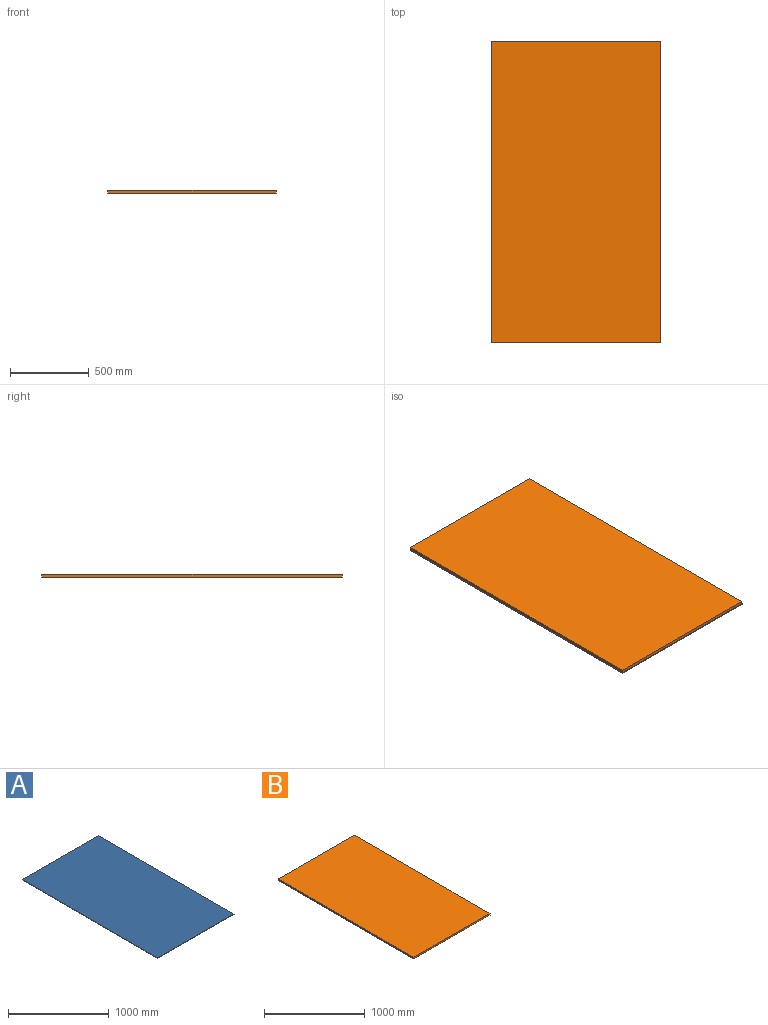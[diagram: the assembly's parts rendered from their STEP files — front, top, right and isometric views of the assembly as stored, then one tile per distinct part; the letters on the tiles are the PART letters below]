
ASSEMBLY  parts=2 mates=1
PART A: 6 faces, bbox 1066.8x1905x5 mm
  f0: plane 1905x5mm, normal (-1,0,0), area 9525mm2, adj f1,f3,f4,f5
  f1: plane 1066.8x5mm, normal (0,-1,0), area 5334mm2, adj f0,f2,f4,f5
  f2: plane 1905x5mm, normal (1,0,0), area 9525mm2, adj f1,f3,f4,f5
  f3: plane 1066.8x5mm, normal (0,1,0), area 5334mm2, adj f0,f2,f4,f5
  f4: plane 1905x1066.8mm, normal (0,0,1), area 2032254mm2, adj f0,f1,f2,f3
  f5: plane 1905x1066.8mm, normal (0,0,-1), area 2032254mm2, adj f0,f1,f2,f3
PART B: 6 faces, bbox 1066.8x1905x18.3 mm
  f0: plane 1905x18.26mm, normal (-1,0,0), area 34780.6mm2, adj f1,f3,f4,f5
  f1: plane 1066.8x18.26mm, normal (0,-1,0), area 19477.1mm2, adj f0,f2,f4,f5
  f2: plane 1905x18.26mm, normal (1,0,0), area 34780.6mm2, adj f1,f3,f4,f5
  f3: plane 1066.8x18.26mm, normal (0,1,0), area 19477.1mm2, adj f0,f2,f4,f5
  f4: plane 1905x1066.8mm, normal (0,0,1), area 2032254mm2, adj f0,f1,f2,f3
  f5: plane 1905x1066.8mm, normal (0,0,-1), area 2032254mm2, adj f0,f1,f2,f3
PLACE A at identity
PLACE B t=(-4.54,2.17,5)mm
MATE fastened B.f5 <-> A.f4  axis (0,0,1) through (-37.62,-61.51,5)mm
